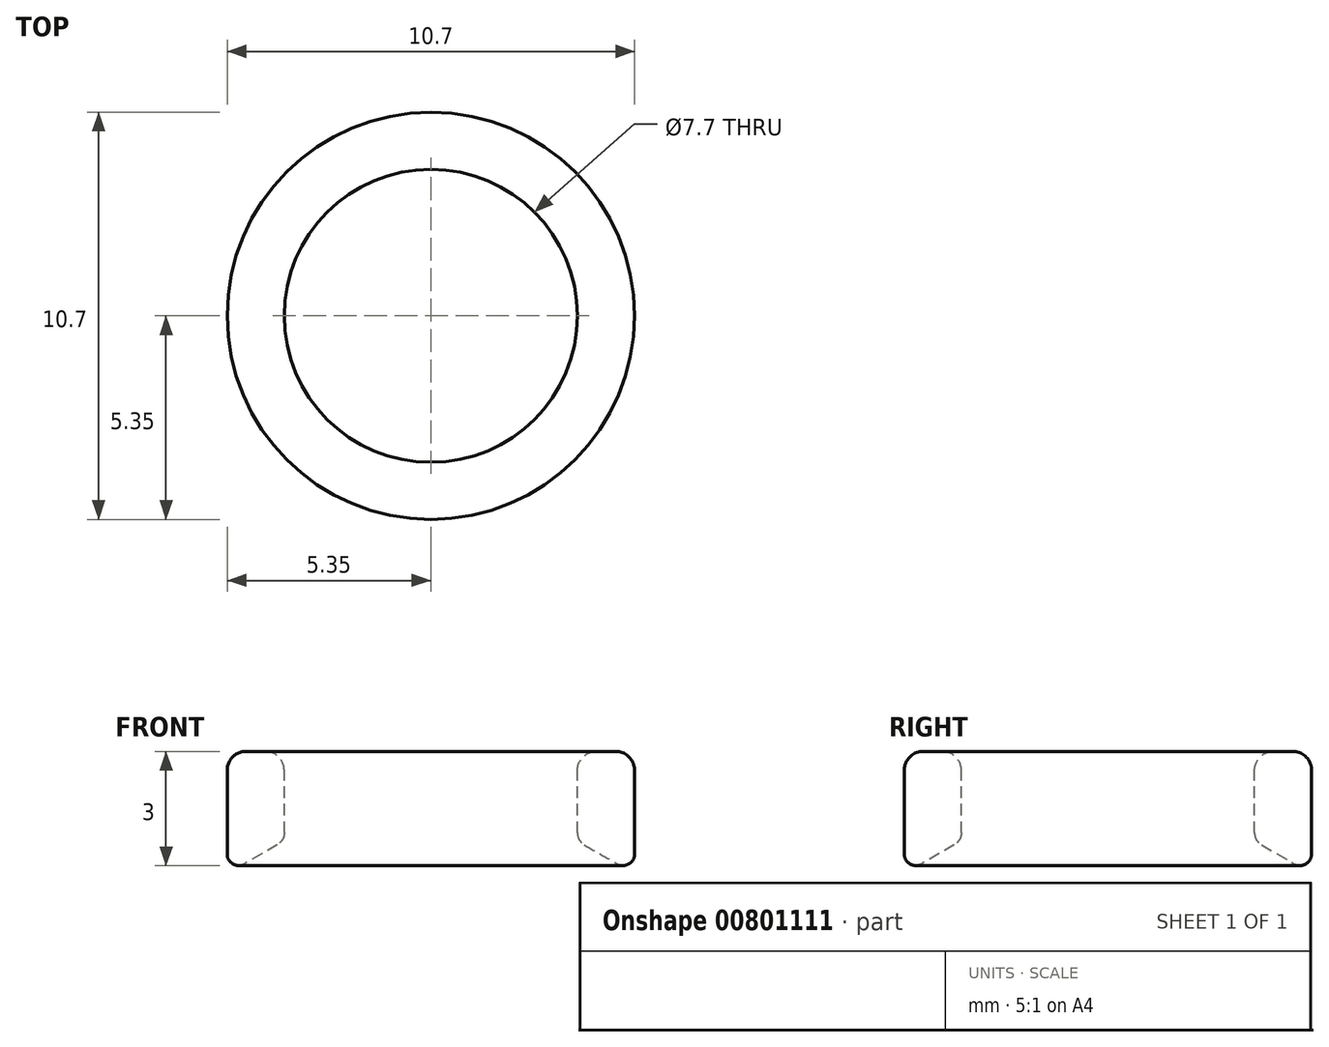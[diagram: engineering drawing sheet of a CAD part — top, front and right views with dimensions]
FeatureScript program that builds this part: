
annotation { "Feature Type Name" : "Feature", "Feature Type Description" : "" }
export const myFeature = defineFeature(function(context is Context, id is Id, definition is map)
    precondition{}
    {
        {
            var Q0;
            Q0=qCreatedBy(makeId("Front.planeOp"),FACE);
            var sketch = newSketch(context, id + "F0", { "sketchPlane" : qUnion([Q0])});
            skLineSegment(sketch, "E0", {"start": v(0, 10.59) * mm, "end": v(0, -11.76) * mm, "construction": true});
            skCircle(sketch, "E1", {"center": v(0, 0) * mm, "radius": 8.5 * mm, "construction": true});
            skCircle(sketch, "E2.0", {"center": v(0, 0) * mm, "radius": 8.2 * mm, "construction": true});
            skLineSegment(sketch, "E3", {"start": v(-4.03, 8.06) * mm, "end": v(-4.9, 7.56) * mm});
            skArc(sketch, "E4", {"start": v(-5.35, 7.82) * mm, "mid": v(-5.2, 7.56) * mm, "end": v(-4.9, 7.56) * mm});
            skLineSegment(sketch, "E5", {"start": v(-5.35, 7.82) * mm, "end": v(-5.35, 10.52) * mm});
            skLineSegment(sketch, "E6", {"start": v(-3.75, 0) * mm, "end": v(-3.75, 14.65) * mm, "construction": true});
            skArc(sketch, "E7", {"start": v(-4.03, 8.06) * mm, "mid": v(-3.9, 8.2) * mm, "end": v(-3.85, 8.38) * mm});
            skLineSegment(sketch, "E8", {"start": v(-3.85, 8.38) * mm, "end": v(-3.85, 10.52) * mm});
            skLineSegment(sketch, "E9", {"start": v(-5.35, 10.52) * mm, "end": v(-3.85, 10.52) * mm});
            skSolve(sketch);
        }
        {
            var Q0;
            Q0=qSketchRegion(id+"F0",true);
            var Q1;
            Q1=sQuery(id+"F0.wireOp",EDGE,"E0");
            revolve(context, id + "F1", {"surfaceOperationType" : NewSurfaceOperationType.NEW, "entities" : qUnion([Q0]), "axis" : qUnion([Q1]), "revolveType" : RevolveType.FULL});
        }
        {
            var Q0;
            Q0=makeQuery(id+"F1.opRevolve","SWEPT_FACE",FACE,{"disambiguationData":[OSD([sQuery(id+"F0.wireOp",EDGE,"E9")])]});
            fillet(context, id + "F2", {"entities" : qUnion([Q0]), "radius" : 0.5 * mm, "tangentPropagation" : true, "allowEdgeOverflow" : false});
        }
    });
